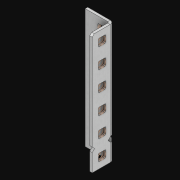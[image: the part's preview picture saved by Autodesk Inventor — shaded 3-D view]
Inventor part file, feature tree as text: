
AUTODESK INVENTOR PART (.ipt)
format: ipt  version: 2021 (Build 250183000, 183)  size: 1,074,688 bytes
history: native  units: in
note: dims shown in document units (in); Inventor stores cm internally (conversion verified against a paired STEP export)
features: extrude x14, other x12, sketch x4, pattern_linear x2, sheet_metal_op x1
ambient origin geometry x8: Origin, YZ Plane, XZ Plane, XY Plane, X Axis, Y Axis, Z Axis, Center Point
bodies: Solid1 (feature_tree)
feature tree (33):
  pattern_linear  "Rectangular Pattern1"  Spacing1=0.5in  [1 undecoded]
  pattern_linear  "Rectangular Pattern3"  Count1=6  [1 undecoded]
  extrude  "Extrusion1"  Depth=0.5in
  extrude  "Extrusion2"  Depth=0.5in
  sketch  "Sketch1"  dims[d0=0.182in]
  other  "Srf1"
  sketch  "Sketch3"  dims[d1=0.063in d2=0.0in]
  other  "Srf3"
  other  "Srf4"
  other  "Srf5"
  other  "Srf6"
  other  "Srf7"
  other  "Srf8"
  other  "Srf142"
  other  "Srf143"
  other  "Srf144"
  other  "Srf145"
  other  "Srf146"
  sketch  "Sketch4"  dims[d6=0.182in]
  sketch  "Sketch5"  dims[d7=0.063in d8=0.0in d11=0.5in d12=0.3937in d14=0.5in d18=2.3622in d20=0.5in d21=14.5in d22=0.0in d23=0.841in d24=0.0in]
  sheet_metal_op  "Fold1"
  extrude  "ExtrusionSrf1"  TaperAngle=0.0deg  [1 undecoded]
  extrude  "ExtrusionSrf3"  Depth=0.5in TaperAngle=0.0deg
  extrude  "ExtrusionSrf4"  [1 undecoded]
  extrude  "ExtrusionSrf5"  [1 undecoded]
  extrude  "ExtrusionSrf6"  [1 undecoded]
  extrude  "ExtrusionSrf7"  [1 undecoded]
  extrude  "ExtrusionSrf8"  [1 undecoded]
  extrude  "ExtrusionSrf142"  [1 undecoded]
  extrude  "ExtrusionSrf143"  [1 undecoded]
  extrude  "ExtrusionSrf144"  [1 undecoded]
  extrude  "ExtrusionSrf145"  [1 undecoded]
  extrude  "ExtrusionSrf146"  [1 undecoded]
note: 13 required parameter values undecoded (feature->parameter linkage not recoverable at this tier; creation-order binding heuristic only, values carry confidence <= 0.55)
